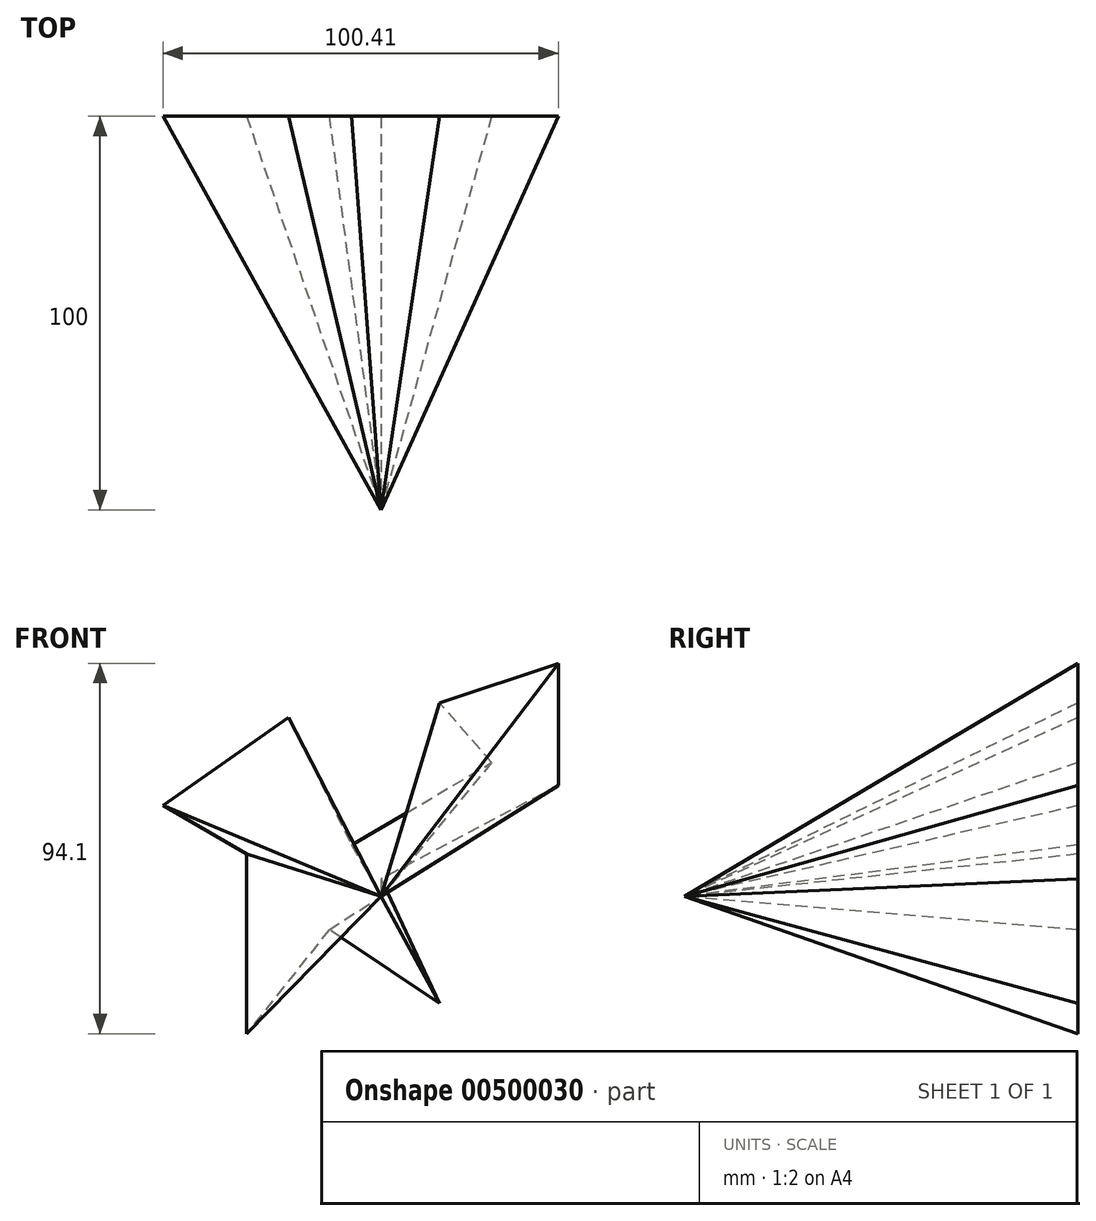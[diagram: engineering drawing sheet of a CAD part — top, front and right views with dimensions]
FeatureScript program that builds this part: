
annotation { "Feature Type Name" : "Feature", "Feature Type Description" : "" }
export const myFeature = defineFeature(function(context is Context, id is Id, definition is map)
    precondition{}
    {
        {
            var Q0;
            Q0=qCreatedBy(makeId("Front.planeOp"),FACE);
            var sketch = newSketch(context, id + "F0", { "sketchPlane" : qUnion([Q0])});
            skLineSegment(sketch, "E0", {"start": v(-55.37, 23.1) * mm, "end": v(-23.52, 45.47) * mm});
            skLineSegment(sketch, "E1", {"start": v(-23.52, 45.47) * mm, "end": v(-7.46, 13.05) * mm});
            skLineSegment(sketch, "E2", {"start": v(-7.46, 13.05) * mm, "end": v(28.11, 34) * mm});
            skLineSegment(sketch, "E3", {"start": v(28.11, 34) * mm, "end": v(14.92, 49.2) * mm});
            skLineSegment(sketch, "E4", {"start": v(14.92, 49.2) * mm, "end": v(45.04, 59.24) * mm});
            skLineSegment(sketch, "E5", {"start": v(45.04, 59.24) * mm, "end": v(45.04, 28.26) * mm});
            skLineSegment(sketch, "E6", {"start": v(45.04, 28.26) * mm, "end": v(0, 4.45) * mm});
            skLineSegment(sketch, "E7", {"start": v(0, 4.45) * mm, "end": v(14.92, -27.11) * mm});
            skLineSegment(sketch, "E8", {"start": v(14.92, -27.11) * mm, "end": v(-13.2, -8.46) * mm});
            skLineSegment(sketch, "E9", {"start": v(-13.2, -8.46) * mm, "end": v(-34.14, -34.86) * mm});
            skLineSegment(sketch, "E10", {"start": v(-34.14, -34.86) * mm, "end": v(-34.14, -5.02) * mm});
            skLineSegment(sketch, "E11", {"start": v(-34.14, -5.02) * mm, "end": v(-34.14, 10.76) * mm});
            skLineSegment(sketch, "E12", {"start": v(-34.14, 10.76) * mm, "end": v(-55.37, 23.1) * mm});
            skSolve(sketch);
        }
        {
            var Q0;
            Q0=qCreatedBy(makeId("Front.planeOp"),FACE);
            cPlane(context, id + "F1", {"entities" : qUnion([Q0]), "cplaneType" : CPlaneType.OFFSET, "offset" : 100 * mm, "width" : 150 * mm, "height" : 150 * mm});
        }
        {
            var Q0;
            Q0=qCreatedBy(id+"F1.planeOp",FACE);
            var sketch = newSketch(context, id + "F2", { "sketchPlane" : qUnion([Q0])});
            skPoint(sketch, "E13", {"position": v(0, 0) * mm});
            skSolve(sketch);
        }
        {
            var Q0;
            Q0=makeQuery(id+"F0.imprint","IMPRINT",FACE,{"disambiguationData":[TD([[makeQuery(id+"F0.imprint","IMPRINT",EDGE,{"derivedFrom":sQuery(id+"F0.wireOp",EDGE,"E0")}),-1.0]])]});
            var Q1;
            Q1=sQuery(id+"F2.wireOp",VERTEX,"E13");
            loft(context, id + "F3", {"sheetProfilesArray" : [{ "sheetProfileEntities" : qUnion([Q0]) }, { "sheetProfileEntities" : qUnion([Q1]) }]});
        }
    });
